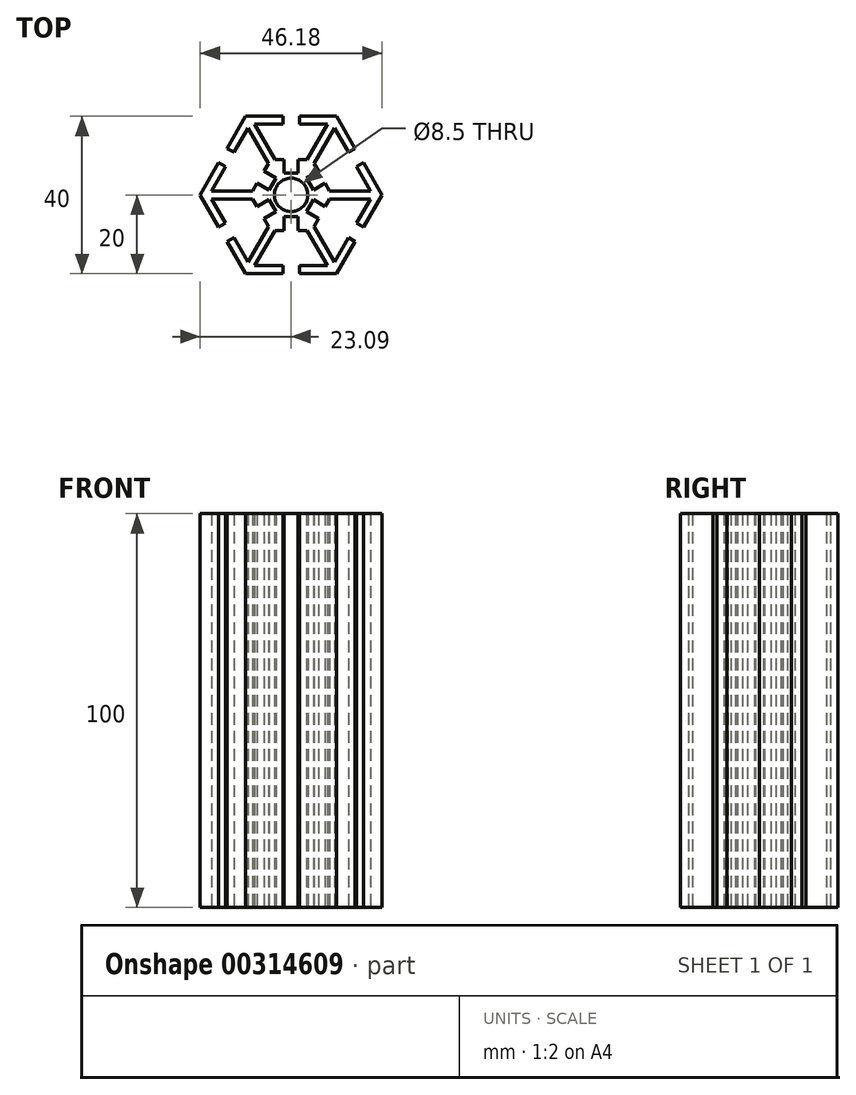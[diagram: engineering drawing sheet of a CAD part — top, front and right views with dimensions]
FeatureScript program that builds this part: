
annotation { "Feature Type Name" : "Feature", "Feature Type Description" : "" }
export const myFeature = defineFeature(function(context is Context, id is Id, definition is map)
    precondition{}
    {
        {
            var Q0;
            Q0=qCreatedBy(makeId("Top.planeOp"),FACE);
            var sketch = newSketch(context, id + "F0", { "sketchPlane" : qUnion([Q0])});
            skArc(sketch, "E0", {"start": v(2.12, 3.68) * mm, "mid": v(0, 4.25) * mm, "end": v(-2.13, 3.68) * mm});
            skLineSegment(sketch, "E1", {"start": v(11.55, 20) * mm, "end": v(2.1, 20) * mm});
            skLineSegment(sketch, "E2.1", {"start": v(-9.24, 18) * mm, "end": v(-4.04, 9) * mm});
            skLineSegment(sketch, "E3.0", {"start": v(9.24, 18) * mm, "end": v(2.1, 18) * mm});
            skLineSegment(sketch, "E4", {"start": v(-2.1, 20) * mm, "end": v(-2.1, 18) * mm});
            skLineSegment(sketch, "E5", {"start": v(2.1, 20) * mm, "end": v(2.1, 18) * mm});
            skLineSegment(sketch, "E6", {"start": v(-4.04, 9) * mm, "end": v(-1.75, 9) * mm});
            skLineSegment(sketch, "E7", {"start": v(-1.75, 9) * mm, "end": v(-1.75, 5.5) * mm});
            skLineSegment(sketch, "E8", {"start": v(-1.75, 5.5) * mm, "end": v(1.75, 5.5) * mm});
            skLineSegment(sketch, "E9", {"start": v(1.75, 5.5) * mm, "end": v(1.75, 9) * mm});
            skLineSegment(sketch, "E10.trimOffspring", {"start": v(-2.1, 20) * mm, "end": v(-11.55, 20) * mm});
            skLineSegment(sketch, "E11.trimOffspring", {"start": v(-2.1, 18) * mm, "end": v(-9.24, 18) * mm});
            skLineSegment(sketch, "E12.trimOffspring", {"start": v(1.75, 9) * mm, "end": v(4.04, 9) * mm});
            skLineSegment(sketch, "E13.trimOffspring", {"start": v(4.04, 9) * mm, "end": v(9.24, 18) * mm});
            skLineSegment(sketch, "E14.1.0", {"start": v(-18.37, 8.18) * mm, "end": v(-23.1, 0) * mm});
            skLineSegment(sketch, "E14.1.1", {"start": v(-18.37, 8.18) * mm, "end": v(-16.64, 7.18) * mm});
            skLineSegment(sketch, "E14.1.2", {"start": v(-16.64, 7.18) * mm, "end": v(-20.2, 1) * mm});
            skLineSegment(sketch, "E14.1.3", {"start": v(-20.2, 1) * mm, "end": v(-9.81, 1) * mm});
            skLineSegment(sketch, "E14.1.4", {"start": v(-9.81, 1) * mm, "end": v(-8.67, 2.98) * mm});
            skLineSegment(sketch, "E14.1.5", {"start": v(-8.67, 2.98) * mm, "end": v(-5.64, 1.23) * mm});
            skLineSegment(sketch, "E14.1.6", {"start": v(-5.64, 1.23) * mm, "end": v(-3.89, 4.27) * mm});
            skArc(sketch, "E14.1.7", {"start": v(-2.13, 3.68) * mm, "mid": v(-3.68, 2.12) * mm, "end": v(-4.25, 0) * mm});
            skLineSegment(sketch, "E14.1.8", {"start": v(-3.89, 4.27) * mm, "end": v(-6.92, 6.02) * mm});
            skLineSegment(sketch, "E14.1.9", {"start": v(-6.92, 6.02) * mm, "end": v(-5.77, 8) * mm});
            skLineSegment(sketch, "E14.1.10", {"start": v(-5.77, 8) * mm, "end": v(-10.97, 17) * mm});
            skLineSegment(sketch, "E14.1.11", {"start": v(-10.97, 17) * mm, "end": v(-14.54, 10.82) * mm});
            skLineSegment(sketch, "E14.1.12", {"start": v(-16.27, 11.82) * mm, "end": v(-14.54, 10.82) * mm});
            skLineSegment(sketch, "E14.1.13", {"start": v(-11.55, 20) * mm, "end": v(-16.27, 11.82) * mm});
            skLineSegment(sketch, "E14.2.0", {"start": v(-16.27, -11.82) * mm, "end": v(-11.55, -20) * mm});
            skLineSegment(sketch, "E14.2.1", {"start": v(-16.27, -11.82) * mm, "end": v(-14.54, -10.82) * mm});
            skLineSegment(sketch, "E14.2.2", {"start": v(-14.54, -10.82) * mm, "end": v(-10.97, -17) * mm});
            skLineSegment(sketch, "E14.2.3", {"start": v(-10.97, -17) * mm, "end": v(-5.77, -8) * mm});
            skLineSegment(sketch, "E14.2.4", {"start": v(-5.77, -8) * mm, "end": v(-6.92, -6.02) * mm});
            skLineSegment(sketch, "E14.2.5", {"start": v(-6.92, -6.02) * mm, "end": v(-3.89, -4.27) * mm});
            skLineSegment(sketch, "E14.2.6", {"start": v(-3.89, -4.27) * mm, "end": v(-5.64, -1.23) * mm});
            skArc(sketch, "E14.2.7", {"start": v(-4.25, 0) * mm, "mid": v(-3.68, -2.13) * mm, "end": v(-2.12, -3.68) * mm});
            skLineSegment(sketch, "E14.2.8", {"start": v(-5.64, -1.23) * mm, "end": v(-8.67, -2.98) * mm});
            skLineSegment(sketch, "E14.2.9", {"start": v(-8.67, -2.98) * mm, "end": v(-9.81, -1) * mm});
            skLineSegment(sketch, "E14.2.10", {"start": v(-9.81, -1) * mm, "end": v(-20.2, -1) * mm});
            skLineSegment(sketch, "E14.2.11", {"start": v(-20.2, -1) * mm, "end": v(-16.64, -7.18) * mm});
            skLineSegment(sketch, "E14.2.12", {"start": v(-18.37, -8.18) * mm, "end": v(-16.64, -7.18) * mm});
            skLineSegment(sketch, "E14.2.13", {"start": v(-23.1, 0) * mm, "end": v(-18.37, -8.18) * mm});
            skLineSegment(sketch, "E14.3.0", {"start": v(2.1, -20) * mm, "end": v(11.55, -20) * mm});
            skLineSegment(sketch, "E14.3.1", {"start": v(2.1, -20) * mm, "end": v(2.1, -18) * mm});
            skLineSegment(sketch, "E14.3.2", {"start": v(2.1, -18) * mm, "end": v(9.24, -18) * mm});
            skLineSegment(sketch, "E14.3.3", {"start": v(9.24, -18) * mm, "end": v(4.04, -9) * mm});
            skLineSegment(sketch, "E14.3.4", {"start": v(4.04, -9) * mm, "end": v(1.75, -9) * mm});
            skLineSegment(sketch, "E14.3.5", {"start": v(1.75, -9) * mm, "end": v(1.75, -5.5) * mm});
            skLineSegment(sketch, "E14.3.6", {"start": v(1.75, -5.5) * mm, "end": v(-1.75, -5.5) * mm});
            skArc(sketch, "E14.3.7", {"start": v(-2.12, -3.68) * mm, "mid": v(0, -4.25) * mm, "end": v(2.13, -3.68) * mm});
            skLineSegment(sketch, "E14.3.8", {"start": v(-1.75, -5.5) * mm, "end": v(-1.75, -9) * mm});
            skLineSegment(sketch, "E14.3.9", {"start": v(-1.75, -9) * mm, "end": v(-4.04, -9) * mm});
            skLineSegment(sketch, "E14.3.10", {"start": v(-4.04, -9) * mm, "end": v(-9.24, -18) * mm});
            skLineSegment(sketch, "E14.3.11", {"start": v(-9.24, -18) * mm, "end": v(-2.1, -18) * mm});
            skLineSegment(sketch, "E14.3.12", {"start": v(-2.1, -20) * mm, "end": v(-2.1, -18) * mm});
            skLineSegment(sketch, "E14.3.13", {"start": v(-11.55, -20) * mm, "end": v(-2.1, -20) * mm});
            skLineSegment(sketch, "E14.4.0", {"start": v(18.37, -8.18) * mm, "end": v(23.1, 0) * mm});
            skLineSegment(sketch, "E14.4.1", {"start": v(18.37, -8.18) * mm, "end": v(16.64, -7.18) * mm});
            skLineSegment(sketch, "E14.4.2", {"start": v(16.64, -7.18) * mm, "end": v(20.2, -1) * mm});
            skLineSegment(sketch, "E14.4.3", {"start": v(20.2, -1) * mm, "end": v(9.81, -1) * mm});
            skLineSegment(sketch, "E14.4.4", {"start": v(9.81, -1) * mm, "end": v(8.67, -2.98) * mm});
            skLineSegment(sketch, "E14.4.5", {"start": v(8.67, -2.98) * mm, "end": v(5.64, -1.23) * mm});
            skLineSegment(sketch, "E14.4.6", {"start": v(5.64, -1.23) * mm, "end": v(3.89, -4.27) * mm});
            skArc(sketch, "E14.4.7", {"start": v(2.13, -3.68) * mm, "mid": v(3.68, -2.13) * mm, "end": v(4.25, 0) * mm});
            skLineSegment(sketch, "E14.4.8", {"start": v(3.89, -4.27) * mm, "end": v(6.92, -6.02) * mm});
            skLineSegment(sketch, "E14.4.9", {"start": v(6.92, -6.02) * mm, "end": v(5.77, -8) * mm});
            skLineSegment(sketch, "E14.4.10", {"start": v(5.77, -8) * mm, "end": v(10.97, -17) * mm});
            skLineSegment(sketch, "E14.4.11", {"start": v(10.97, -17) * mm, "end": v(14.54, -10.82) * mm});
            skLineSegment(sketch, "E14.4.12", {"start": v(16.27, -11.82) * mm, "end": v(14.54, -10.82) * mm});
            skLineSegment(sketch, "E14.4.13", {"start": v(11.55, -20) * mm, "end": v(16.27, -11.82) * mm});
            skLineSegment(sketch, "E14.5.0", {"start": v(16.27, 11.82) * mm, "end": v(11.55, 20) * mm});
            skLineSegment(sketch, "E14.5.1", {"start": v(16.27, 11.82) * mm, "end": v(14.54, 10.82) * mm});
            skLineSegment(sketch, "E14.5.2", {"start": v(14.54, 10.82) * mm, "end": v(10.97, 17) * mm});
            skLineSegment(sketch, "E14.5.3", {"start": v(10.97, 17) * mm, "end": v(5.77, 8) * mm});
            skLineSegment(sketch, "E14.5.4", {"start": v(5.77, 8) * mm, "end": v(6.92, 6.02) * mm});
            skLineSegment(sketch, "E14.5.5", {"start": v(6.92, 6.02) * mm, "end": v(3.89, 4.27) * mm});
            skLineSegment(sketch, "E14.5.6", {"start": v(3.89, 4.27) * mm, "end": v(5.64, 1.23) * mm});
            skArc(sketch, "E14.5.7", {"start": v(4.25, 0) * mm, "mid": v(3.68, 2.13) * mm, "end": v(2.12, 3.68) * mm});
            skLineSegment(sketch, "E14.5.8", {"start": v(5.64, 1.23) * mm, "end": v(8.67, 2.98) * mm});
            skLineSegment(sketch, "E14.5.9", {"start": v(8.67, 2.98) * mm, "end": v(9.81, 1) * mm});
            skLineSegment(sketch, "E14.5.10", {"start": v(9.81, 1) * mm, "end": v(20.2, 1) * mm});
            skLineSegment(sketch, "E14.5.11", {"start": v(20.2, 1) * mm, "end": v(16.64, 7.18) * mm});
            skLineSegment(sketch, "E14.5.12", {"start": v(18.37, 8.18) * mm, "end": v(16.64, 7.18) * mm});
            skLineSegment(sketch, "E14.5.13", {"start": v(23.1, 0) * mm, "end": v(18.37, 8.18) * mm});
            skSolve(sketch);
        }
        {
            var Q0;
            Q0 = qSketchRegion(id + "F0", true);
            extrude(context, id + "F1", {"entities" : qUnion([Q0]), "depth" : 100 * mm});
        }
    });
